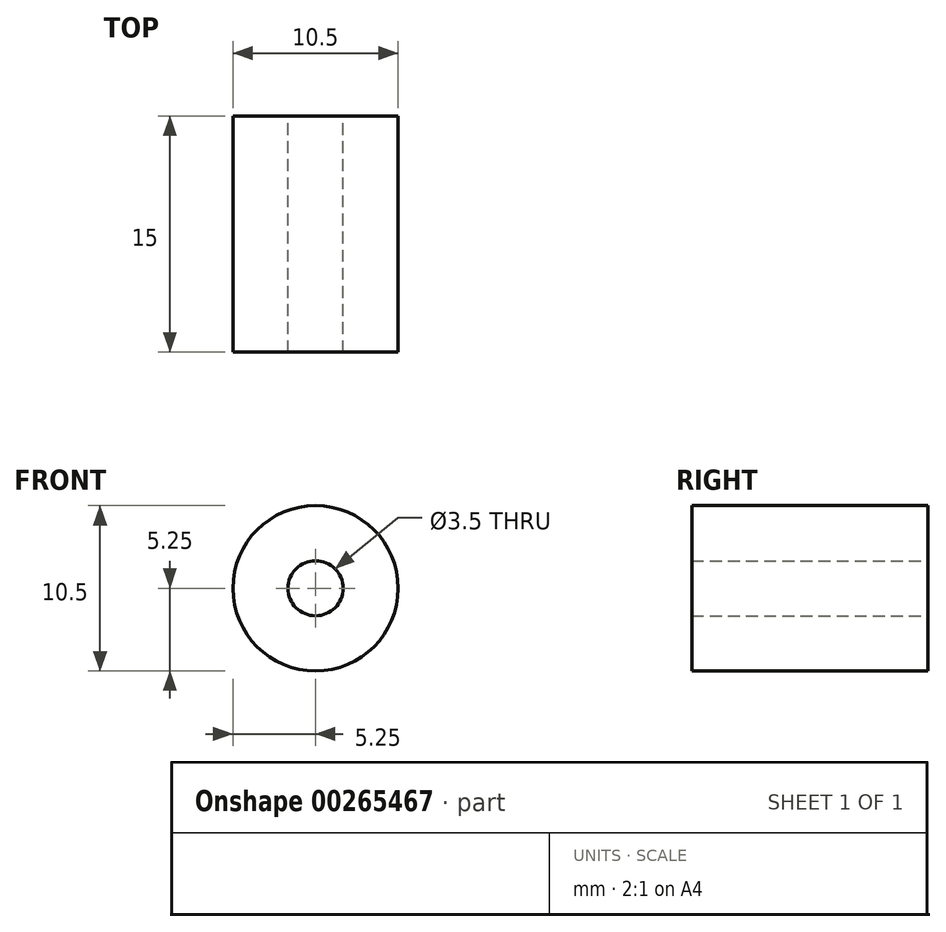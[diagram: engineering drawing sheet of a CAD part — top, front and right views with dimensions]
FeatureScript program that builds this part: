
annotation { "Feature Type Name" : "Feature", "Feature Type Description" : "" }
export const myFeature = defineFeature(function(context is Context, id is Id, definition is map)
    precondition{}
    {
        {
            var Q0;
            Q0=qCreatedBy(makeId("Front.planeOp"),FACE);
            var sketch = newSketch(context, id + "F0", { "sketchPlane" : qUnion([Q0])});
            skCircle(sketch, "E0", {"center": v(0, 0) * mm, "radius": 1.75 * mm});
            skCircle(sketch, "E1", {"center": v(0, 0) * mm, "radius": 5.25 * mm});
            skSolve(sketch);
        }
        {
            var Q0;
            Q0=makeQuery(id+"F0.imprint","IMPRINT",FACE,{"disambiguationData":[TD([[makeQuery(id+"F0.imprint","IMPRINT",EDGE,{"derivedFrom":sQuery(id+"F0.wireOp",EDGE,"E0")}),-1.0]])]});
            extrude(context, id + "F1", {"entities" : qUnion([Q0]), "depth" : 15 * mm});
        }
    });
